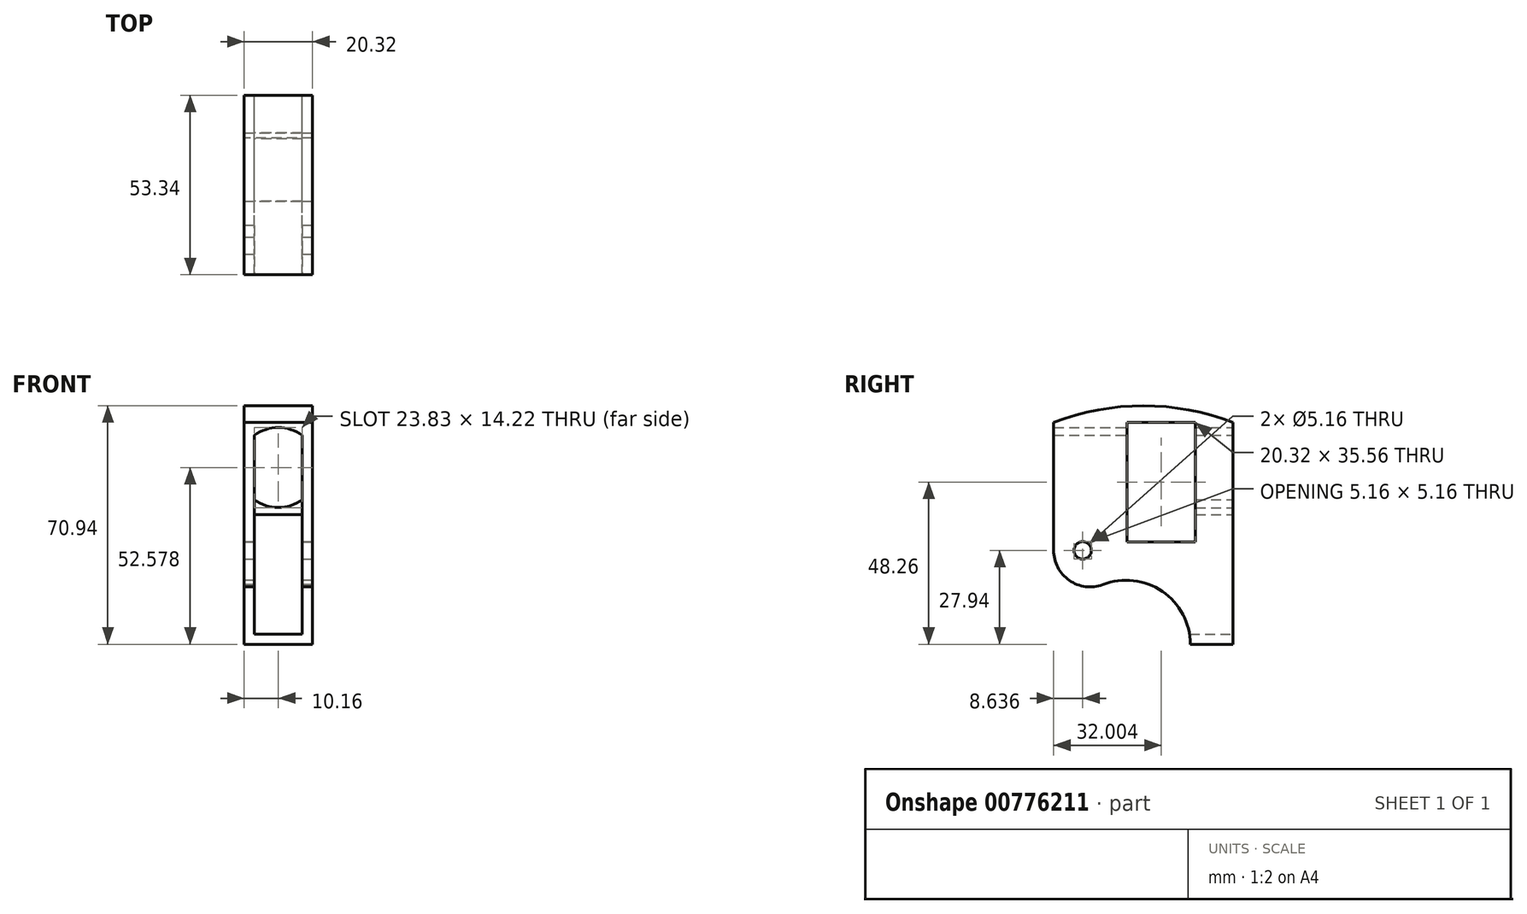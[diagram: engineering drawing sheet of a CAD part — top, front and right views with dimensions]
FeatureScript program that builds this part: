
annotation { "Feature Type Name" : "Feature", "Feature Type Description" : "" }
export const myFeature = defineFeature(function(context is Context, id is Id, definition is map)
    precondition{}
    {
        {
            var Q0;
            Q0=qCreatedBy(makeId("Right.planeOp"),FACE);
            var sketch = newSketch(context, id + "F0", { "sketchPlane" : qUnion([Q0])});
            skLineSegment(sketch, "E0", {"start": v(0, 0) * mm, "end": v(0, 66.04) * mm});
            skLineSegment(sketch, "E1", {"start": v(-45.44, 71.12) * mm, "end": v(43.94, 71.12) * mm, "construction": true});
            skLineSegment(sketch, "E2", {"start": v(-53.34, 27.94) * mm, "end": v(-53.34, 66.04) * mm});
            skArc(sketch, "E3", {"start": v(0, 66.04) * mm, "mid": v(-26.67, 70.94) * mm, "end": v(-53.34, 66.04) * mm});
            skLineSegment(sketch, "E4", {"start": v(0, 0) * mm, "end": v(-12.7, 0) * mm});
            skLineSegment(sketch, "E5", {"start": v(-44.7, 42.38) * mm, "end": v(-44.7, 13.5) * mm, "construction": true});
            skLineSegment(sketch, "E6", {"start": v(-70.94, 27.94) * mm, "end": v(-5.4, 27.94) * mm, "construction": true});
            skLineSegment(sketch, "E7", {"start": v(57.14, 0) * mm, "end": v(-85.19, 0) * mm, "construction": true});
            skPoint(sketch, "E8", {"position": v(-44.7, 27.94) * mm});
            skLineSegment(sketch, "E9", {"start": v(-31.75, -9.15) * mm, "end": v(-31.75, 8.4) * mm, "construction": true});
            skArc(sketch, "E10", {"start": v(-12.7, 0) * mm, "mid": v(-21.03, 15.75) * mm, "end": v(-38.74, 17.72) * mm});
            skPoint(sketch, "E10.centerSnap0", {"position": v(-31.75, -0.37) * mm});
            skPoint(sketch, "E11.orphan", {"position": v(-53.34, 27.94) * mm});
            skArc(sketch, "E12", {"start": v(-53.34, 27.94) * mm, "mid": v(-48.55, 18.93) * mm, "end": v(-38.4, 17.85) * mm});
            skSolve(sketch);
        }
        {
            var Q0;
            Q0=makeQuery(id+"F0.imprint","IMPRINT",FACE,{"disambiguationData":[TD([[makeQuery(id+"F0.imprint","IMPRINT",EDGE,{"derivedFrom":sQuery(id+"F0.wireOp",EDGE,"E0")}),1.0]])]});
            extrude(context, id + "F1", {"entities" : qUnion([Q0]), "depth" : 10.16 * mm, "offsetDistance" : 25.4 * mm, "hasSecondDirection" : true, "secondDirectionOppositeDirection" : true, "secondDirectionDepth" : 10.16 * mm});
        }
        {
            var Q0;
            Q0=makeQuery(id+"F1.opExtrude","CAP_FACE",FACE,{"disambiguationData":[OSD([sQuery(id+"F0.wireOp",EDGE,"E0"),sQuery(id+"F0.wireOp",EDGE,"E2"),sQuery(id+"F0.wireOp",EDGE,"E3"),sQuery(id+"F0.wireOp",EDGE,"E4"),sQuery(id+"F0.wireOp",EDGE,"E10"),sQuery(id+"F0.wireOp",EDGE,"E12")])],"isStart":false});
            var sketch = newSketch(context, id + "F2", { "sketchPlane" : qUnion([Q0])});
            skLineSegment(sketch, "E13", {"start": v(0, -6.67) * mm, "end": v(0, 72.64) * mm, "construction": true});
            skLineSegment(sketch, "E14", {"start": v(9.37, 0) * mm, "end": v(-71.11, 0) * mm, "construction": true});
            skLineSegment(sketch, "E15", {"start": v(-49.04, 27.94) * mm, "end": v(-39.51, 27.94) * mm, "construction": true});
            skLineSegment(sketch, "E16", {"start": v(-44.7, 24.47) * mm, "end": v(-44.7, 31.71) * mm, "construction": true});
            skCircle(sketch, "E17", {"center": v(-44.7, 27.94) * mm, "radius": 2.58 * mm});
            skPoint(sketch, "E17.centerSnap0", {"position": v(-44.7, 28.1) * mm});
            skLineSegment(sketch, "E18", {"start": v(-31.5, 30.48) * mm, "end": v(-11.18, 30.48) * mm});
            skLineSegment(sketch, "E19", {"start": v(-11.18, 30.48) * mm, "end": v(-11.18, 66.04) * mm});
            skLineSegment(sketch, "E20", {"start": v(-11.18, 66.04) * mm, "end": v(-31.5, 66.04) * mm});
            skLineSegment(sketch, "E21", {"start": v(-31.5, 66.04) * mm, "end": v(-31.5, 30.48) * mm});
            skSolve(sketch);
        }
        {
            var Q0;
            Q0=makeQuery(id+"F2.imprint","IMPRINT",FACE,{"disambiguationData":[TD([[makeQuery(id+"F2.imprint","IMPRINT",EDGE,{"derivedFrom":sQuery(id+"F2.wireOp",EDGE,"E18")}),1.0]])]});
            var Q1;
            Q1=makeQuery(id+"F2.imprint","IMPRINT",FACE,{"disambiguationData":[TD([[makeQuery(id+"F2.imprint","IMPRINT",EDGE,{"derivedFrom":sQuery(id+"F2.wireOp",EDGE,"E17")}),1.0]])]});
            extrude(context, id + "F3", {"entities" : qUnion([Q0, Q1]), "operationType" : NewBodyOperationType.REMOVE, "oppositeDirection" : true, "depth" : 25.4 * mm, "offsetDistance" : 25.4 * mm});
        }
        {
            var Q0;
            Q0=makeQuery(id+"F1.opExtrude","SWEPT_FACE",FACE,{"disambiguationData":[OSD([sQuery(id+"F0.wireOp",EDGE,"E0")])]});
            var sketch = newSketch(context, id + "F4", { "sketchPlane" : qUnion([Q0])});
            skLineSegment(sketch, "E22", {"start": v(-9.42, 3.05) * mm, "end": v(9.03, 3.05) * mm});
            skLineSegment(sketch, "E23", {"start": v(0, -1.45) * mm, "end": v(0, 64.35) * mm, "construction": true});
            skLineSegment(sketch, "E24", {"start": v(-7.11, 3.05) * mm, "end": v(-7.11, 38.6) * mm});
            skLineSegment(sketch, "E25.MirrorCS", {"start": v(7.11, 3.05) * mm, "end": v(7.11, 38.6) * mm});
            skLineSegment(sketch, "E26", {"start": v(-7.11, 38.6) * mm, "end": v(7.11, 38.6) * mm});
            skLineSegment(sketch, "E27", {"start": v(-4.02, 52.58) * mm, "end": v(3.62, 52.58) * mm, "construction": true});
            skArc(sketch, "E28", {"start": v(7.11, 62.13) * mm, "mid": v(0, 64.5) * mm, "end": v(-7.11, 62.13) * mm});
            skPoint(sketch, "E28.centerSnap0", {"position": v(-0.2, 52.58) * mm});
            skPoint(sketch, "E29.orphan", {"position": v(7.11, 57.05) * mm});
            skPoint(sketch, "E30.orphan", {"position": v(-7.11, 57.05) * mm});
            skLineSegment(sketch, "E31.trimOffspring", {"start": v(-7.11, 43.02) * mm, "end": v(-7.11, 62.13) * mm});
            skLineSegment(sketch, "E32.trimOffspring", {"start": v(7.11, 43.02) * mm, "end": v(7.11, 62.13) * mm});
            skArc(sketch, "E33.trimOffspring", {"start": v(-7.11, 43.02) * mm, "mid": v(0, 40.67) * mm, "end": v(7.11, 43.02) * mm});
            skSolve(sketch);
        }
        {
            var Q0;
            Q0=makeQuery(id+"F4.imprint","IMPRINT",FACE,{"disambiguationData":[TD([[makeQuery(id+"F4.imprint","IMPRINT",EDGE,{"derivedFrom":sQuery(id+"F4.wireOp",EDGE,"E28")}),1.0]])]});
            var Q1;
            {var subQ0=sQuery(id+"F4.wireOp",EDGE,"E24");Q1=makeQuery(id+"F4.imprint","IMPRINT",FACE,{"disambiguationData":[TD([[makeQuery(id+"F4.imprint","IMPRINT",EDGE,{"derivedFrom":subQ0}),-1.0]])]});}
            extrude(context, id + "F5", {"entities" : qUnion([Q0, Q1]), "operationType" : NewBodyOperationType.REMOVE, "oppositeDirection" : true, "depth" : 54.6 * mm, "offsetDistance" : 25.4 * mm});
        }
        {
            var Q0;
            Q0=makeQuery(id+"F1.opExtrude","SWEPT_FACE",FACE,{"disambiguationData":[OSD([sQuery(id+"F0.wireOp",EDGE,"E2")])]});
            var sketch = newSketch(context, id + "F6", { "sketchPlane" : qUnion([Q0])});
            skLineSegment(sketch, "E34", {"start": v(-7.11, 38.6) * mm, "end": v(7.11, 38.6) * mm});
            skLineSegment(sketch, "E35", {"start": v(7.11, 38.6) * mm, "end": v(7.11, 43.44) * mm});
            skLineSegment(sketch, "E36", {"start": v(-7.11, 38.6) * mm, "end": v(-7.11, 43.44) * mm});
            skArc(sketch, "E37", {"start": v(-7.11, 43.44) * mm, "mid": v(0, 41) * mm, "end": v(7.11, 43.44) * mm});
            skSolve(sketch);
        }
        {
            var Q0;
            {var subQ0=sQuery(id+"F6.wireOp",EDGE,"E34");Q0=makeQuery(id+"F6.imprint","IMPRINT",FACE,{"disambiguationData":[TD([[makeQuery(id+"F6.imprint","IMPRINT",EDGE,{"derivedFrom":subQ0}),1.0]])]});}
            extrude(context, id + "F7", {"entities" : qUnion([Q0]), "operationType" : NewBodyOperationType.REMOVE, "oppositeDirection" : true, "depth" : 25.4 * mm, "offsetDistance" : 25.4 * mm});
        }
    });
